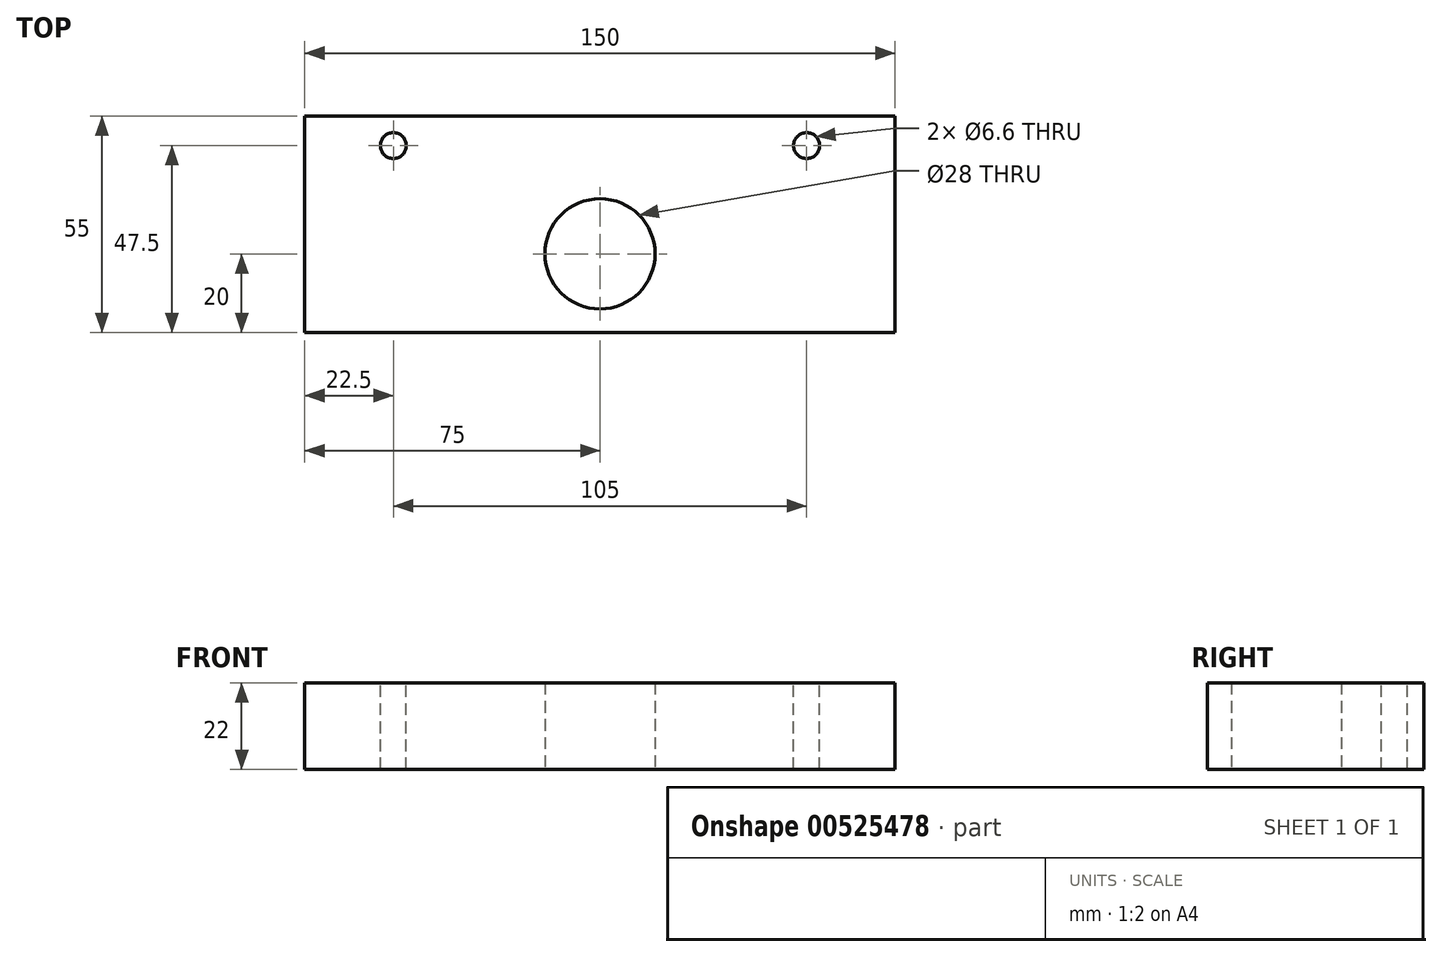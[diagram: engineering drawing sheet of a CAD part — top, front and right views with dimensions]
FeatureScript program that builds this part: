
annotation { "Feature Type Name" : "Feature", "Feature Type Description" : "" }
export const myFeature = defineFeature(function(context is Context, id is Id, definition is map)
    precondition{}
    {
        {
            var Q0;
            Q0=qCreatedBy(makeId("Top.planeOp"),FACE);
            var sketch = newSketch(context, id + "F0", { "sketchPlane" : qUnion([Q0])});
            skLineSegment(sketch, "E0.bottom", {"start": v(75, 27.5) * mm, "end": v(-75, 27.5) * mm});
            skLineSegment(sketch, "E0.top", {"start": v(75, -27.5) * mm, "end": v(-75, -27.5) * mm});
            skLineSegment(sketch, "E0.left", {"start": v(75, 27.5) * mm, "end": v(75, -27.5) * mm});
            skLineSegment(sketch, "E0.right", {"start": v(-75, 27.5) * mm, "end": v(-75, -27.5) * mm});
            skPoint(sketch, "E1", {"position": v(0, -7.5) * mm});
            skSolve(sketch);
        }
        {
            var Q0;
            Q0=makeQuery(id+"F0.imprint","IMPRINT",FACE,{"disambiguationData":[TD([[makeQuery(id+"F0.imprint","IMPRINT",EDGE,{"derivedFrom":sQuery(id+"F0.wireOp",EDGE,"E0.bottom")}),1.0]])]});
            extrude(context, id + "F1", {"entities" : qUnion([Q0]), "depth" : 22 * mm, "offsetDistance" : 25 * mm});
        }
        {
            var Q0;
            Q0=makeQuery(id+"F1.opExtrude","CAP_FACE",FACE,{"disambiguationData":[OSD([sQuery(id+"F0.wireOp",EDGE,"E0.bottom"),sQuery(id+"F0.wireOp",EDGE,"E0.top"),sQuery(id+"F0.wireOp",EDGE,"E0.left"),sQuery(id+"F0.wireOp",EDGE,"E0.right")])],"isStart":false});
            var sketch = newSketch(context, id + "F2", { "sketchPlane" : qUnion([Q0])});
            skPoint(sketch, "E2", {"position": v(-52.5, 20) * mm});
            skPoint(sketch, "E3", {"position": v(52.5, 20) * mm});
            skSolve(sketch);
        }
        {
            var Q0;
            Q0=sQuery(id+"F2.wireOp",VERTEX,"E2");
            var Q1;
            Q1=sQuery(id+"F2.wireOp",VERTEX,"E3");
            var Q2;
            Q2=makeQuery(id+"F1.opExtrude","SWEPT_BODY",BODY,{"disambiguationData":[OSD([sQuery(id+"F0.wireOp",EDGE,"E0.bottom"),sQuery(id+"F0.wireOp",EDGE,"E0.top"),sQuery(id+"F0.wireOp",EDGE,"E0.left"),sQuery(id+"F0.wireOp",EDGE,"E0.right")])]});
            hole(context, id + "F3", {"style" : HoleStyle.SIMPLE, "endStyle" : HoleEndStyle.THROUGH, "standardTappedOrClearance" : lookupTablePath({ "standard" : "ISO", "fit" : "Normal", "size" : "M6", "type" : "Clearance" }), "standardBlindInLast" : lookupTablePath({ "fit" : "Standard", "standard" : "ISO", "size" : "M6", "type" : "Clearance" }), "holeDiameter" : 6.6 * mm, "isTappedThrough" : true, "tappedDepth" : 12 * mm, "tapClearance" : 3, "locations" : qUnion([Q0, Q1]), "scope" : qUnion([Q2])});
        }
        {
            var Q0;
            Q0=sQuery(id+"F0.wireOp",VERTEX,"E1");
            var Q1;
            Q1=makeQuery(id+"F1.opExtrude","SWEPT_BODY",BODY,{"disambiguationData":[OSD([sQuery(id+"F0.wireOp",EDGE,"E0.bottom"),sQuery(id+"F0.wireOp",EDGE,"E0.top"),sQuery(id+"F0.wireOp",EDGE,"E0.left"),sQuery(id+"F0.wireOp",EDGE,"E0.right")])]});
            hole(context, id + "F4", {"style" : HoleStyle.SIMPLE, "endStyle" : HoleEndStyle.THROUGH, "oppositeDirection" : true, "holeDiameter" : 28 * mm, "isTappedThrough" : true, "tappedDepth" : 12 * mm, "tapClearance" : 3, "locations" : qUnion([Q0]), "scope" : qUnion([Q1])});
        }
    });
